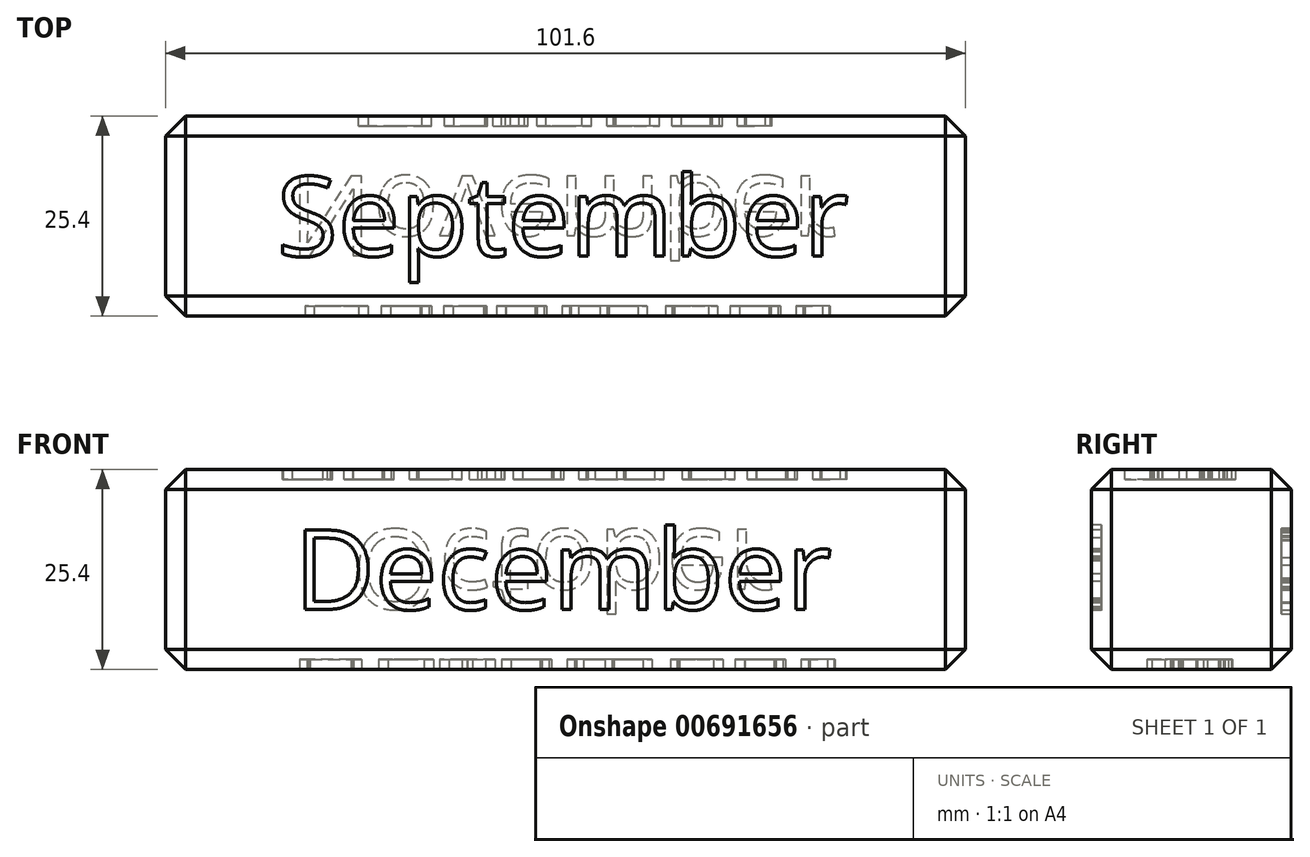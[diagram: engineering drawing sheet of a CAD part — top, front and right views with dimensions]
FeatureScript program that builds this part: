
annotation { "Feature Type Name" : "Feature", "Feature Type Description" : "" }
export const myFeature = defineFeature(function(context is Context, id is Id, definition is map)
    precondition{}
    {
        {
            var Q0;
            Q0=qCreatedBy(makeId("Top.planeOp"),FACE);
            var sketch = newSketch(context, id + "F0", { "sketchPlane" : qUnion([Q0])});
            skLineSegment(sketch, "E0.bottom", {"start": v(50.8, 12.7) * mm, "end": v(-50.8, 12.7) * mm});
            skLineSegment(sketch, "E0.top", {"start": v(50.8, -12.7) * mm, "end": v(-50.8, -12.7) * mm});
            skLineSegment(sketch, "E0.left", {"start": v(50.8, 12.7) * mm, "end": v(50.8, -12.7) * mm});
            skLineSegment(sketch, "E0.right", {"start": v(-50.8, 12.7) * mm, "end": v(-50.8, -12.7) * mm});
            skPoint(sketch, "E0.middle", {"position": v(0, 0) * mm});
            skSolve(sketch);
        }
        {
            var Q0;
            Q0 = qSketchRegion(id + "F0", true);
            extrude(context, id + "F1", {"entities" : qUnion([Q0]), "depth" : 12.7 * mm, "offsetDistance" : 25.4 * mm, "hasSecondDirection" : true, "secondDirectionOppositeDirection" : true, "secondDirectionDepth" : 12.7 * mm});
        }
        {
            var Q0;
            Q0=makeQuery(id+"F1.opExtrude","SWEPT_FACE",FACE,{"disambiguationData":[OSD([sQuery(id+"F0.wireOp",EDGE,"E0.right")])]});
            var Q1;
            Q1=makeQuery(id+"F1.opExtrude","CAP_FACE",FACE,{"disambiguationData":[OSD([sQuery(id+"F0.wireOp",EDGE,"E0.bottom"),sQuery(id+"F0.wireOp",EDGE,"E0.top"),sQuery(id+"F0.wireOp",EDGE,"E0.left"),sQuery(id+"F0.wireOp",EDGE,"E0.right")])],"isStart":false});
            var Q2;
            Q2=makeQuery(id+"F1.opExtrude","SWEPT_FACE",FACE,{"disambiguationData":[OSD([sQuery(id+"F0.wireOp",EDGE,"E0.top")])]});
            var Q3;
            Q3=makeQuery(id+"F1.opExtrude","SWEPT_FACE",FACE,{"disambiguationData":[OSD([sQuery(id+"F0.wireOp",EDGE,"E0.left")])]});
            var Q4;
            Q4=makeQuery(id+"F1.opExtrude","CAP_FACE",FACE,{"disambiguationData":[OSD([sQuery(id+"F0.wireOp",EDGE,"E0.bottom"),sQuery(id+"F0.wireOp",EDGE,"E0.top"),sQuery(id+"F0.wireOp",EDGE,"E0.left"),sQuery(id+"F0.wireOp",EDGE,"E0.right")])],"isStart":true});
            chamfer(context, id + "F2", {"entities" : qUnion([Q0, Q1, Q2, Q3, Q4]), "width" : 2.54 * mm, "tangentPropagation" : true});
        }
        {
            var Q0;
            Q0=makeQuery(id+"F1.opExtrude","CAP_FACE",FACE,{"disambiguationData":[OSD([sQuery(id+"F0.wireOp",EDGE,"E0.bottom"),sQuery(id+"F0.wireOp",EDGE,"E0.top"),sQuery(id+"F0.wireOp",EDGE,"E0.left"),sQuery(id+"F0.wireOp",EDGE,"E0.right")])],"isStart":false});
            var sketch = newSketch(context, id + "F3", { "sketchPlane" : qUnion([Q0])});
            skText(sketch, "E1", { "text": "September", "fontName": "OpenSans-Regular.ttf"});
            skLineSegment(sketch, "E2", {"start": v(-57.2, 0) * mm, "end": v(-36.69, 0) * mm, "construction": true});
            const initialGuessF3  = {"E1": [-0.03669, -0.00508, 1, 0, 0.01016]};
            skSetInitialGuess(sketch, initialGuessF3);
            skSolve(sketch);
        }
        {
            var Q0;
            Q0 = qSketchRegion(id + "F3", true);
            extrude(context, id + "F4", {"entities" : qUnion([Q0]), "operationType" : NewBodyOperationType.REMOVE, "oppositeDirection" : true, "depth" : 1.27 * mm, "offsetDistance" : 25.4 * mm});
        }
        {
            var Q0;
            Q0=makeQuery(id+"F1.opExtrude","SWEPT_FACE",FACE,{"disambiguationData":[OSD([sQuery(id+"F0.wireOp",EDGE,"E0.bottom")])]});
            var sketch = newSketch(context, id + "F5", { "sketchPlane" : qUnion([Q0])});
            skText(sketch, "E3", { "text": "October", "fontName": "OpenSans-Regular.ttf"});
            skLineSegment(sketch, "E4", {"start": v(62.13, 0) * mm, "end": v(27.13, 0) * mm, "construction": true});
            const initialGuessF5  = {"E3": [0.02713, 0.00508, -1, 0, 0.01016]};
            skSetInitialGuess(sketch, initialGuessF5);
            skSolve(sketch);
        }
        {
            var Q0;
            Q0 = qSketchRegion(id + "F5", true);
            extrude(context, id + "F6", {"entities" : qUnion([Q0]), "operationType" : NewBodyOperationType.REMOVE, "oppositeDirection" : true, "depth" : 1.27 * mm, "offsetDistance" : 25.4 * mm});
        }
        {
            var Q0;
            Q0=makeQuery(id+"F1.opExtrude","CAP_FACE",FACE,{"disambiguationData":[OSD([sQuery(id+"F0.wireOp",EDGE,"E0.bottom"),sQuery(id+"F0.wireOp",EDGE,"E0.top"),sQuery(id+"F0.wireOp",EDGE,"E0.left"),sQuery(id+"F0.wireOp",EDGE,"E0.right")])],"isStart":true});
            var sketch = newSketch(context, id + "F7", { "sketchPlane" : qUnion([Q0])});
            skText(sketch, "E5", { "text": "November", "fontName": "OpenSans-Regular.ttf"});
            skLineSegment(sketch, "E6", {"start": v(-35.16, 0) * mm, "end": v(-67.47, 0) * mm, "construction": true});
            const initialGuessF7  = {"E5": [-0.03516, -0.00508, 1, 0, 0.01016]};
            skSetInitialGuess(sketch, initialGuessF7);
            skSolve(sketch);
        }
        {
            var Q0;
            Q0 = qSketchRegion(id + "F7", true);
            extrude(context, id + "F8", {"entities" : qUnion([Q0]), "operationType" : NewBodyOperationType.REMOVE, "oppositeDirection" : true, "depth" : 1.27 * mm, "offsetDistance" : 25.4 * mm});
        }
        {
            var Q0;
            Q0=makeQuery(id+"F1.opExtrude","SWEPT_FACE",FACE,{"disambiguationData":[OSD([sQuery(id+"F0.wireOp",EDGE,"E0.top")])]});
            var sketch = newSketch(context, id + "F9", { "sketchPlane" : qUnion([Q0])});
            skText(sketch, "E7", { "text": "December", "fontName": "OpenSans-Regular.ttf"});
            skLineSegment(sketch, "E8", {"start": v(-34.5, 0) * mm, "end": v(-64.66, 0) * mm, "construction": true});
            const initialGuessF9  = {"E7": [-0.0345, -0.00508, 1, 0, 0.01016]};
            skSetInitialGuess(sketch, initialGuessF9);
            skSolve(sketch);
        }
        {
            var Q0;
            Q0 = qSketchRegion(id + "F9", true);
            extrude(context, id + "F10", {"entities" : qUnion([Q0]), "operationType" : NewBodyOperationType.REMOVE, "oppositeDirection" : true, "depth" : 1.27 * mm, "offsetDistance" : 25.4 * mm});
        }
    });
